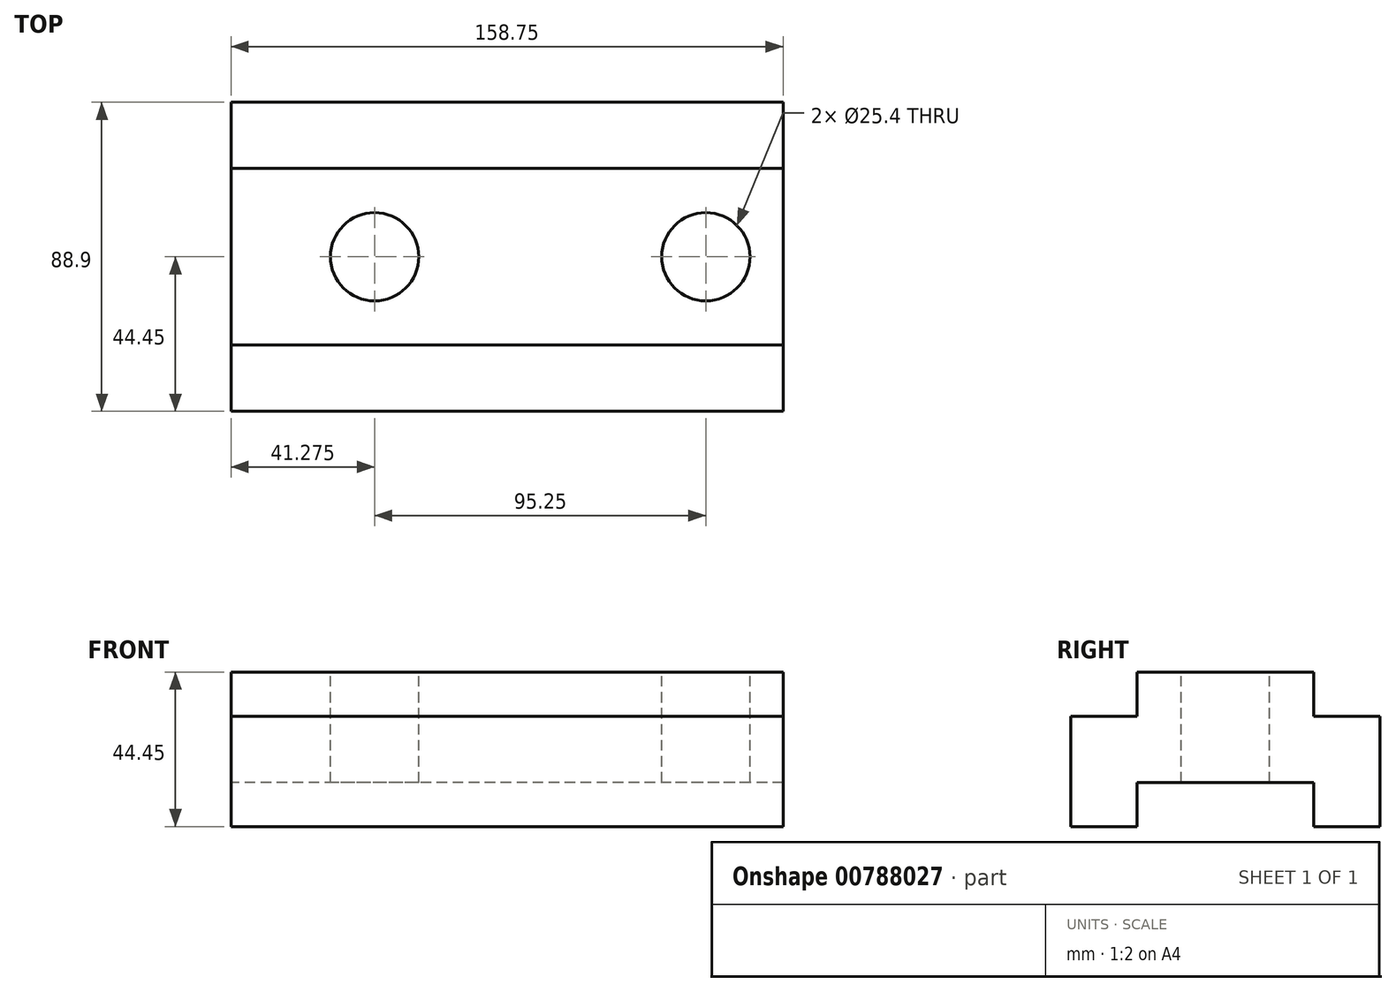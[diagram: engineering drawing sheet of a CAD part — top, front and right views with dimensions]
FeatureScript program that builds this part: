
annotation { "Feature Type Name" : "Feature", "Feature Type Description" : "" }
export const myFeature = defineFeature(function(context is Context, id is Id, definition is map)
    precondition{}
    {
        {
            var Q0;
            Q0=qCreatedBy(makeId("Right.planeOp"),FACE);
            var sketch = newSketch(context, id + "F0", { "sketchPlane" : qUnion([Q0])});
            skLineSegment(sketch, "E0", {"start": v(0, 0) * mm, "end": v(19.05, 0) * mm});
            skLineSegment(sketch, "E1", {"start": v(19.05, 0) * mm, "end": v(19.05, 12.7) * mm});
            skLineSegment(sketch, "E2", {"start": v(19.05, 12.7) * mm, "end": v(69.85, 12.7) * mm});
            skLineSegment(sketch, "E3", {"start": v(69.85, 12.7) * mm, "end": v(69.85, 0) * mm});
            skLineSegment(sketch, "E4", {"start": v(69.85, 0) * mm, "end": v(88.9, 0) * mm});
            skLineSegment(sketch, "E5", {"start": v(88.9, 0) * mm, "end": v(88.9, 31.75) * mm});
            skLineSegment(sketch, "E6", {"start": v(88.9, 31.75) * mm, "end": v(69.85, 31.75) * mm});
            skLineSegment(sketch, "E7", {"start": v(69.85, 31.75) * mm, "end": v(69.85, 44.45) * mm});
            skLineSegment(sketch, "E8", {"start": v(69.85, 44.45) * mm, "end": v(19.05, 44.45) * mm});
            skLineSegment(sketch, "E9", {"start": v(19.05, 44.45) * mm, "end": v(19.05, 31.75) * mm});
            skLineSegment(sketch, "E10", {"start": v(19.05, 31.75) * mm, "end": v(0, 31.75) * mm});
            skLineSegment(sketch, "E11", {"start": v(0, 31.75) * mm, "end": v(0, 0) * mm});
            skSolve(sketch);
        }
        {
            var Q0;
            Q0=makeQuery(id+"F0.imprint","IMPRINT",FACE,{"disambiguationData":[TD([[makeQuery(id+"F0.imprint","IMPRINT",EDGE,{"derivedFrom":sQuery(id+"F0.wireOp",EDGE,"E0")}),1.0]])]});
            extrude(context, id + "F1", {"entities" : qUnion([Q0]), "depth" : 158.75 * mm, "offsetDistance" : 25.4 * mm});
        }
        {
            var Q0;
            Q0=makeQuery(id+"F1.opExtrude","SWEPT_FACE",FACE,{"disambiguationData":[OSD([sQuery(id+"F0.wireOp",EDGE,"E8")])]});
            var sketch = newSketch(context, id + "F2", { "sketchPlane" : qUnion([Q0])});
            skLineSegment(sketch, "E12", {"start": v(0, 44.45) * mm, "end": v(41.28, 44.45) * mm, "construction": true});
            skLineSegment(sketch, "E13", {"start": v(41.28, 44.45) * mm, "end": v(136.53, 44.45) * mm, "construction": true});
            skCircle(sketch, "E14", {"center": v(41.28, 44.45) * mm, "radius": 12.7 * mm});
            skCircle(sketch, "E15", {"center": v(136.53, 44.45) * mm, "radius": 12.7 * mm});
            skSolve(sketch);
        }
        {
            var Q0;
            Q0=makeQuery(id+"F2.imprint","IMPRINT",FACE,{"disambiguationData":[TD([[makeQuery(id+"F2.imprint","IMPRINT",EDGE,{"derivedFrom":sQuery(id+"F2.wireOp",EDGE,"E14")}),1.0]])]});
            var Q1;
            Q1=makeQuery(id+"F2.imprint","IMPRINT",FACE,{"disambiguationData":[TD([[makeQuery(id+"F2.imprint","IMPRINT",EDGE,{"derivedFrom":sQuery(id+"F2.wireOp",EDGE,"E15")}),1.0]])]});
            extrude(context, id + "F3", {"entities" : qUnion([Q0, Q1]), "operationType" : NewBodyOperationType.REMOVE, "endBound" : BoundingType.UP_TO_NEXT, "oppositeDirection" : true, "depth" : 25.4 * mm, "offsetDistance" : 25.4 * mm});
        }
    });
